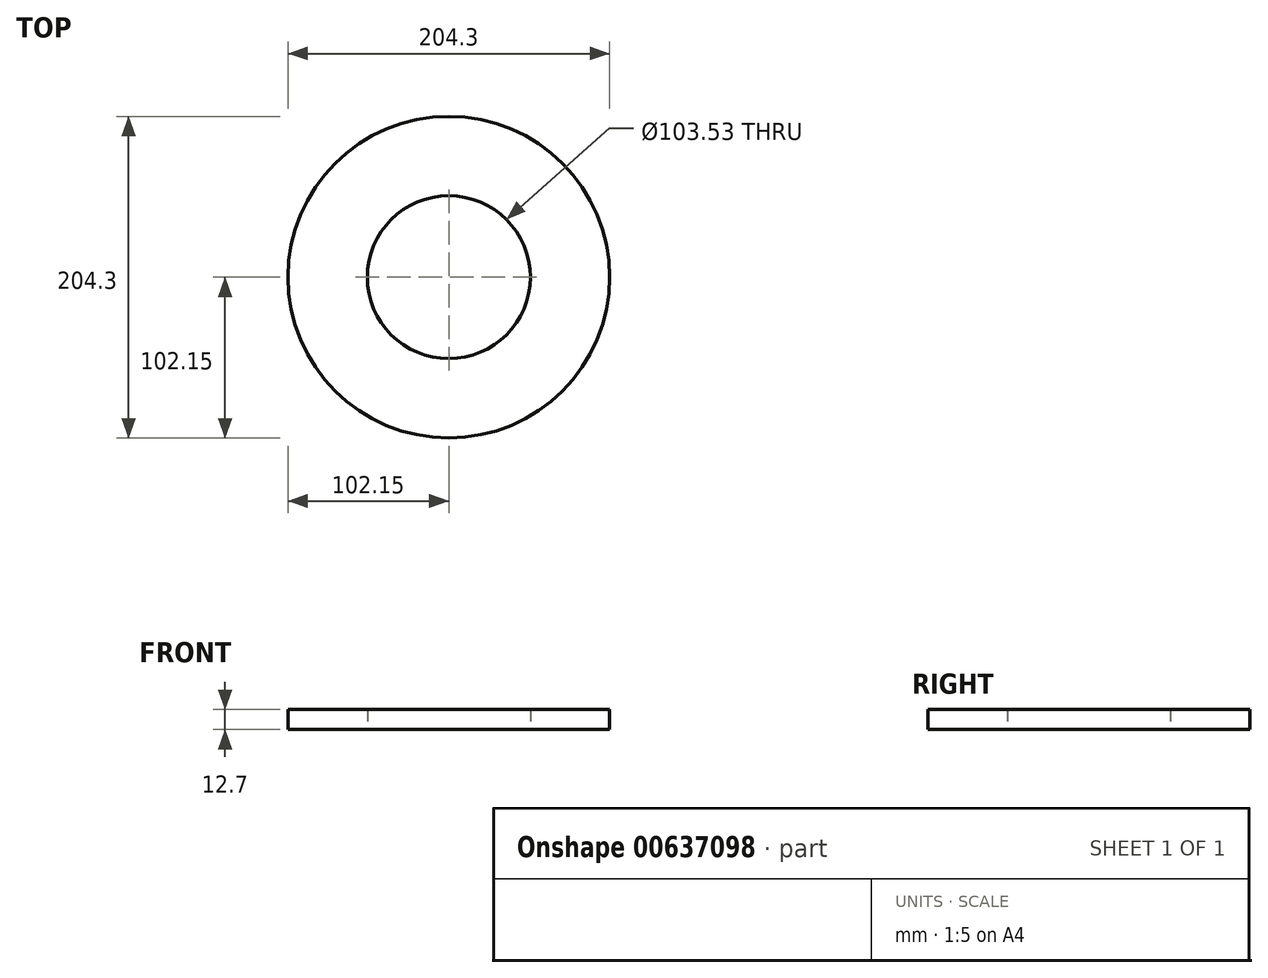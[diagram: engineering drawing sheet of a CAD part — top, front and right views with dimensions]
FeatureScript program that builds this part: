
annotation { "Feature Type Name" : "Feature", "Feature Type Description" : "" }
export const myFeature = defineFeature(function(context is Context, id is Id, definition is map)
    precondition{}
    {
        {
            var Q0;
            Q0=qCreatedBy(makeId("Top.planeOp"),FACE);
            var sketch = newSketch(context, id + "F0", { "sketchPlane" : qUnion([Q0])});
            skCircle(sketch, "E0", {"center": v(0, 0) * mm, "radius": 102.15 * mm});
            skCircle(sketch, "E1", {"center": v(0, 0) * mm, "radius": 51.76 * mm});
            skSolve(sketch);
        }
        {
            var Q0;
            Q0 = qSketchRegion(id + "F0", true);
            extrude(context, id + "F1", {"entities" : qUnion([Q0]), "depth" : 12.7 * mm, "offsetDistance" : 25.4 * mm});
        }
    });
